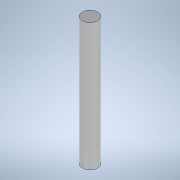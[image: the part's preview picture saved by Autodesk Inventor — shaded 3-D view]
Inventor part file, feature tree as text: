
AUTODESK INVENTOR PART (.ipt)
format: ipt  version: 2020.3 (Build 243373000, 373)  size: 90,112 bytes
history: native  units: mm
features: other x1, extrude x1, sketch x1
ambient origin geometry x8: Origin, YZ Plane, XZ Plane, XY Plane, X Axis, Y Axis, Z Axis, Center Point
bodies: Body1 (feature_tree)
feature tree (3):
  other  "ソリッド1"
  extrude  "押し出し1"  Depth=4.0mm
  sketch  "スケッチ1"
